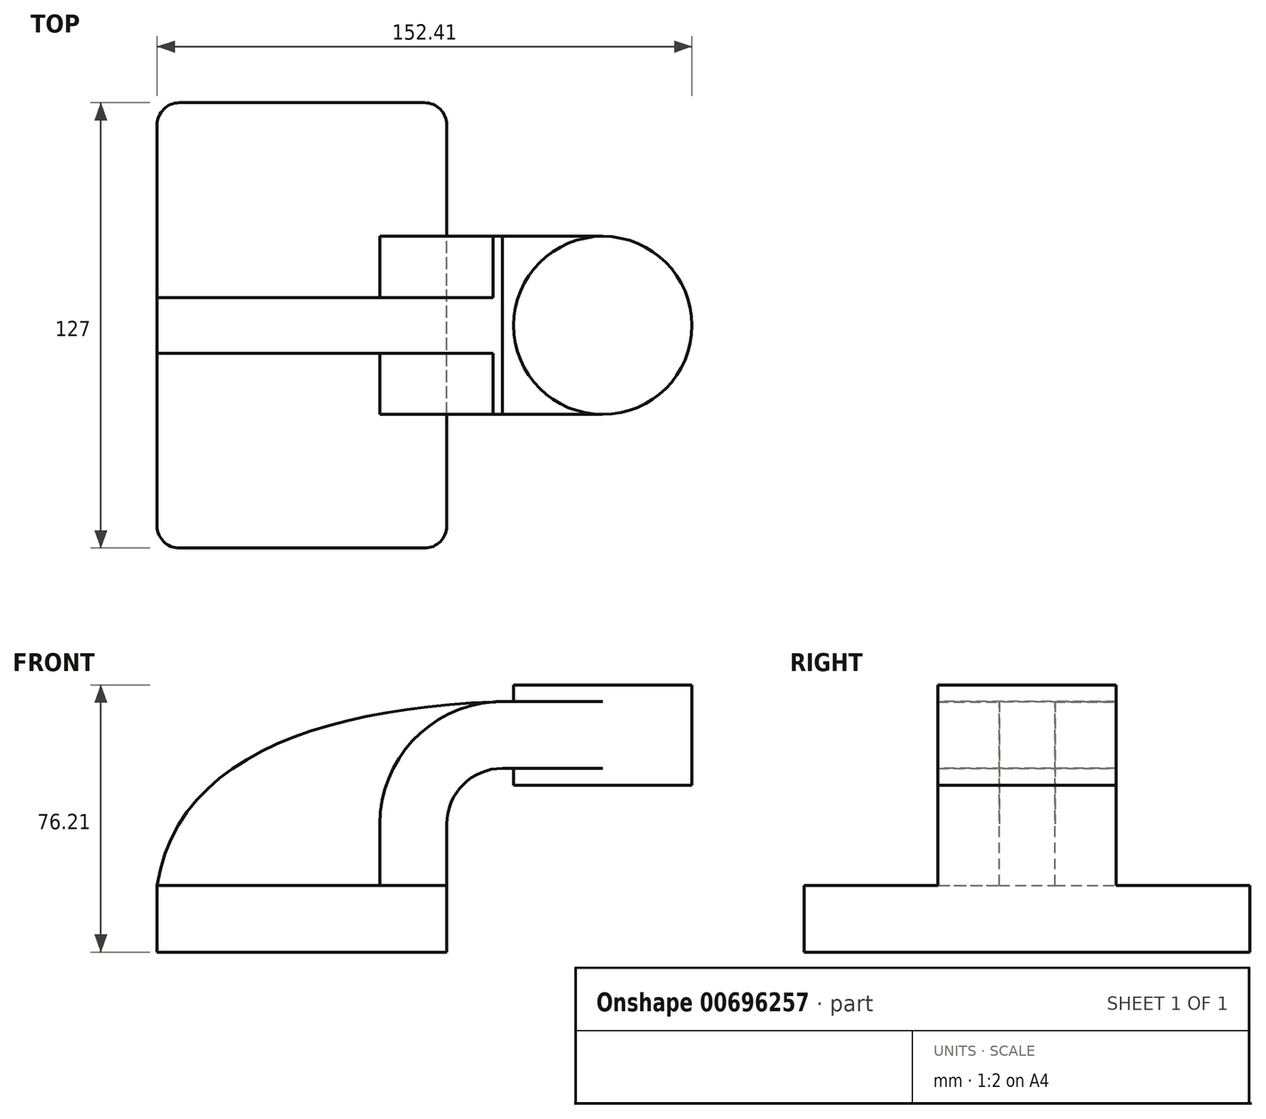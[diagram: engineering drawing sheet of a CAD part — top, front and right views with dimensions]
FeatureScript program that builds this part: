
annotation { "Feature Type Name" : "Feature", "Feature Type Description" : "" }
export const myFeature = defineFeature(function(context is Context, id is Id, definition is map)
    precondition{}
    {
        {
            var Q0;
            Q0=qCreatedBy(makeId("Front.planeOp"),FACE);
            var sketch = newSketch(context, id + "F0", { "sketchPlane" : qUnion([Q0])});
            skLineSegment(sketch, "E0.bottom", {"start": v(-41.28, 9.52) * mm, "end": v(41.28, 9.52) * mm});
            skLineSegment(sketch, "E0.top", {"start": v(-41.28, -9.52) * mm, "end": v(41.28, -9.52) * mm});
            skLineSegment(sketch, "E0.left", {"start": v(-41.28, 9.52) * mm, "end": v(-41.28, -9.52) * mm});
            skLineSegment(sketch, "E0.right", {"start": v(41.28, 9.52) * mm, "end": v(41.28, -9.52) * mm});
            skPoint(sketch, "E0.middle", {"position": v(0, 0) * mm});
            skLineSegment(sketch, "E1.bottom", {"start": v(111.12, 66.68) * mm, "end": v(60.32, 66.68) * mm});
            skLineSegment(sketch, "E1.top", {"start": v(111.12, 38.1) * mm, "end": v(60.32, 38.1) * mm});
            skLineSegment(sketch, "E1.left", {"start": v(111.12, 66.67) * mm, "end": v(111.12, 38.1) * mm});
            skLineSegment(sketch, "E1.right", {"start": v(60.32, 66.67) * mm, "end": v(60.32, 38.1) * mm});
            skPoint(sketch, "E1.middle", {"position": v(85.72, 52.39) * mm});
            skLineSegment(sketch, "E2", {"start": v(41.28, 9.52) * mm, "end": v(41.28, 27) * mm});
            skArc(sketch, "E3", {"start": v(41.28, 27) * mm, "mid": v(45.92, 38.23) * mm, "end": v(57.15, 42.88) * mm});
            skLineSegment(sketch, "E4", {"start": v(57.15, 42.88) * mm, "end": v(85.72, 42.88) * mm});
            skLineSegment(sketch, "E5.0", {"start": v(57.15, 61.93) * mm, "end": v(85.72, 61.93) * mm});
            skArc(sketch, "E5.1", {"start": v(22.23, 27) * mm, "mid": v(32.45, 51.7) * mm, "end": v(57.15, 61.93) * mm});
            skLineSegment(sketch, "E5.2", {"start": v(22.23, 9.52) * mm, "end": v(22.23, 27) * mm});
            skLineSegment(sketch, "E6", {"start": v(85.72, 38.1) * mm, "end": v(85.72, 66.68) * mm});
            skLineSegment(sketch, "E7", {"start": v(85.72, 66.68) * mm, "end": v(85.72, 38.1) * mm});
            skFitSpline(sketch, "E8", {"points": [v(-41.28, 9.52) * mm, v(57.15, 61.93) * mm], "startDerivative": vector(17.48, 112.98) * mm, "endDerivative": vector(148.34, 5.1) * mm});
            skSolve(sketch);
        }
        {
            var Q0;
            Q0=makeQuery(id+"F0.imprint","IMPRINT",FACE,{"disambiguationData":[TD([[makeQuery(id+"F0.imprint","IMPRINT",EDGE,{"derivedFrom":sQuery(id+"F0.wireOp",EDGE,"E0.top")}),1.0]])]});
            extrude(context, id + "F1", {"entities" : qUnion([Q0]), "endBound" : BoundingType.SYMMETRIC, "depth" : 127 * mm, "offsetDistance" : 25.4 * mm});
        }
        {
            var Q0;
            {var subQ1=sQuery(id+"F0.wireOp",EDGE,"E2");Q0=makeQuery(id+"F0.imprint","IMPRINT",FACE,{"disambiguationData":[TD([[makeQuery(id+"F0.imprint","IMPRINT",EDGE,{"derivedFrom":subQ1}),1.0]])]});}
            var Q1;
            {var subQ0=sQuery(id+"F0.wireOp",EDGE,"E5.0");var subQ1=sQuery(id+"F0.wireOp",EDGE,"E1.right");var subQ2=makeQuery(id+"F0.imprint","INTERSECT",VERTEX,{"derivedFrom":[subQ1,subQ0]});Q1=makeQuery(id+"F0.imprint","IMPRINT",FACE,{"disambiguationData":[TD([[makeQuery(id+"F0.imprint","IMPRINT",EDGE,{"disambiguationData":[TD([[subQ2,-1.0]])],"derivedFrom":subQ1}),1.0]])]});}
            extrude(context, id + "F2", {"entities" : qUnion([Q0, Q1]), "operationType" : NewBodyOperationType.ADD, "endBound" : BoundingType.SYMMETRIC, "depth" : 50.8 * mm, "offsetDistance" : 25.4 * mm});
        }
        {
            var Q0;
            {var subQ3=sQuery(id+"F0.wireOp",EDGE,"E5.2");Q0=makeQuery(id+"F0.imprint","IMPRINT",FACE,{"disambiguationData":[TD([[makeQuery(id+"F0.imprint","IMPRINT",EDGE,{"derivedFrom":subQ3}),1.0]])]});}
            extrude(context, id + "F3", {"entities" : qUnion([Q0]), "operationType" : NewBodyOperationType.ADD, "endBound" : BoundingType.SYMMETRIC, "depth" : 15.88 * mm, "offsetDistance" : 25.4 * mm});
        }
        {
            var Q0;
            {var subQ0=sQuery(id+"F0.wireOp",EDGE,"E1.left");Q0=makeQuery(id+"F0.imprint","IMPRINT",FACE,{"disambiguationData":[TD([[makeQuery(id+"F0.imprint","IMPRINT",EDGE,{"derivedFrom":subQ0}),-1.0]])]});}
            var Q1;
            Q1=sQuery(id+"F0.wireOp",EDGE,"E7");
            revolve(context, id + "F4", {"operationType" : NewBodyOperationType.ADD, "entities" : qUnion([Q0]), "axis" : qUnion([Q1]), "revolveType" : RevolveType.FULL});
        }
        {
            var Q0;
            Q0=makeQuery(id+"F1.opExtrude","CAP_EDGE",EDGE,{"disambiguationData":[OSD([sQuery(id+"F0.wireOp",EDGE,"E0.left")])],"isStart":false});
            var Q1;
            Q1=makeQuery(id+"F1.opExtrude","CAP_EDGE",EDGE,{"disambiguationData":[OSD([sQuery(id+"F0.wireOp",EDGE,"E0.right")])],"isStart":false});
            var Q2;
            Q2=makeQuery(id+"F1.opExtrude","CAP_EDGE",EDGE,{"disambiguationData":[OSD([sQuery(id+"F0.wireOp",EDGE,"E0.right")])],"isStart":true});
            var Q3;
            Q3=makeQuery(id+"F1.opExtrude","CAP_EDGE",EDGE,{"disambiguationData":[OSD([sQuery(id+"F0.wireOp",EDGE,"E0.left")])],"isStart":true});
            fillet(context, id + "F5", {"entities" : qUnion([Q0, Q1, Q2, Q3]), "radius" : 6.35 * mm, "tangentPropagation" : true, "allowEdgeOverflow" : false});
        }
    });
